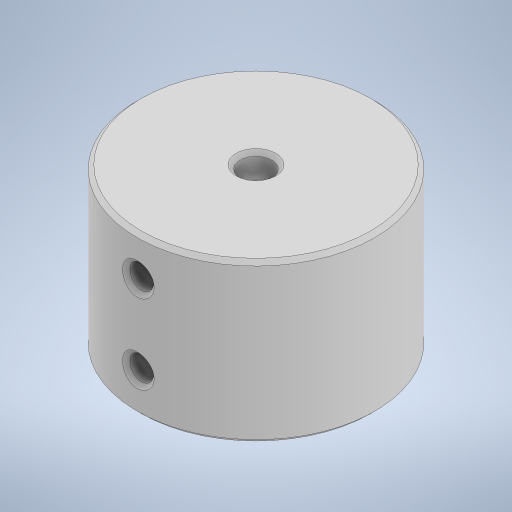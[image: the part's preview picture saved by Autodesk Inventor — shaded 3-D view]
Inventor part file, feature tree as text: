
AUTODESK INVENTOR PART (.ipt)
format: ipt  version: 2023 (Build 270158000, 158)  size: 292,352 bytes
history: native  units: mm
features: extrude x3, sketch x3, other x1, chamfer x1
ambient origin geometry x8: Origin, YZ Plane, XZ Plane, XY Plane, X Axis, Y Axis, Z Axis, Center Point
bodies: Body1 (feature_tree)
feature tree (8):
  other  "Твердое тело1"
  extrude  "Выдавливание1"  Depth=25.0mm
  extrude  "Выдавливание2"  Depth=30.0mm
  extrude  "Выдавливание3"  Depth=10.0mm TaperAngle=0.0deg
  chamfer  "Фаска1"  Distance=4.0mm
  sketch  "Эскиз1"
  sketch  "Эскиз2"
  sketch  "Эскиз3"
